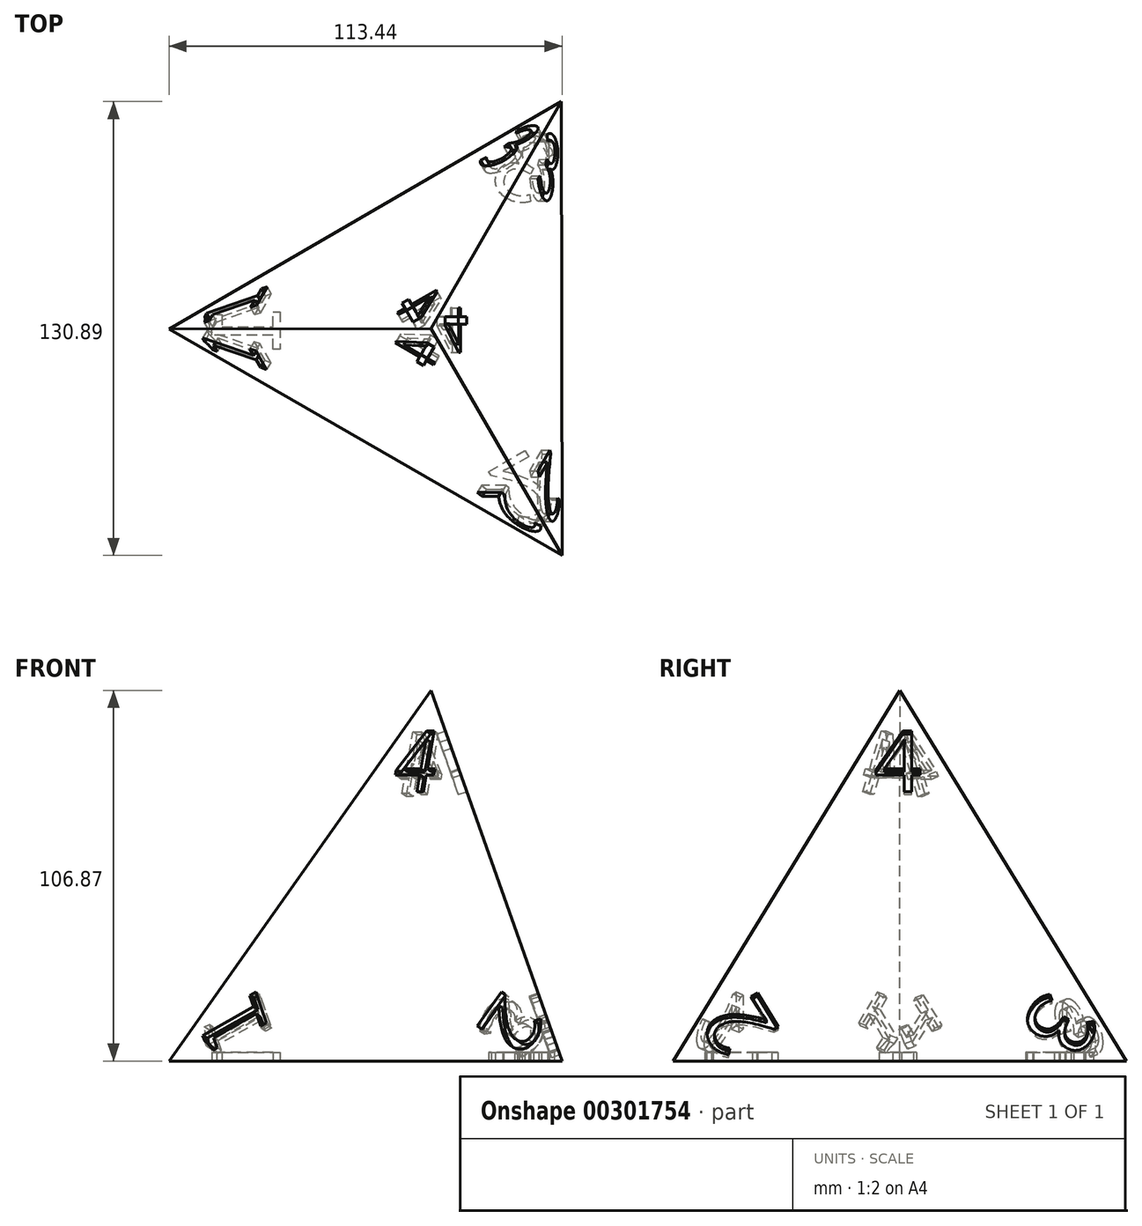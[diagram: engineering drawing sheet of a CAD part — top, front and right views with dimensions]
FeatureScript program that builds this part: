
annotation { "Feature Type Name" : "Feature", "Feature Type Description" : "" }
export const myFeature = defineFeature(function(context is Context, id is Id, definition is map)
    precondition{}
    {
        {
            var Q0;
            Q0=qCreatedBy(makeId("Top.planeOp"),FACE);
            var sketch = newSketch(context, id + "F0", { "sketchPlane" : qUnion([Q0])});
            skCircle(sketch, "E0.cCircle", {"center": v(0, 0) * mm, "radius": 75.57 * mm, "construction": true});
            skLineSegment(sketch, "E0.0", {"start": v(37.87, -65.4) * mm, "end": v(-75.57, -0.1) * mm});
            skLineSegment(sketch, "E0.1", {"start": v(-75.57, -0.1) * mm, "end": v(37.7, 65.5) * mm});
            skLineSegment(sketch, "E0.2", {"start": v(37.7, 65.5) * mm, "end": v(37.87, -65.4) * mm});
            skSolve(sketch);
        }
        {
            var Q0;
            Q0=qCreatedBy(makeId("Top.planeOp"),FACE);
            cPlane(context, id + "F1", {"entities" : qUnion([Q0]), "cplaneType" : CPlaneType.OFFSET, "offset" : 113.36 * mm, "width" : 152.4 * mm, "height" : 152.4 * mm});
        }
        {
            var Q0;
            Q0 = qSketchRegion(id + "F0", true);
            extrude(context, id + "F2", {"entities" : qUnion([Q0]), "depth" : 127 * mm, "hasDraft" : true, "draftAngle" : 19.47 * degree, "draftPullDirection" : true});
        }
        {
            var Q0;
            Q0=makeQuery(id+"F2.opExtrude","SWEPT_FACE",FACE,{"disambiguationData":[OSD([sQuery(id+"F0.wireOp",EDGE,"E0.2")])]});
            var sketch = newSketch(context, id + "F3", { "sketchPlane" : qUnion([Q0])});
            skText(sketch, "E1", { "text": "3", "fontName": "NotoSansCJKkr-Regular.otf"});
            skText(sketch, "E2", { "text": "4", "fontName": "NotoSansCJKkr-Regular.otf"});
            skText(sketch, "E3", { "text": "2", "fontName": "NotoSansCJKkr-Regular.otf"});
            const initialGuessF3  = {"E1": [0.04163, 0.00963, -0.49963, -0.86624, 0.01902], "E2": [-0.00737, 0.06982, 1, 0, 0.01824], "E3": [-0.03448, -0.0032, -0.50037, 0.86581, 0.01882]};
            skSetInitialGuess(sketch, initialGuessF3);
            skSolve(sketch);
        }
        {
            var Q0;
            Q0 = qSketchRegion(id + "F3", true);
            extrude(context, id + "F4", {"entities" : qUnion([Q0]), "operationType" : NewBodyOperationType.REMOVE, "oppositeDirection" : true, "depth" : 2.54 * mm});
        }
        {
            var Q0;
            Q0=makeQuery(id+"F2.opExtrude","CAP_FACE",FACE,{"disambiguationData":[OSD([sQuery(id+"F0.wireOp",EDGE,"E0.0"),sQuery(id+"F0.wireOp",EDGE,"E0.1"),sQuery(id+"F0.wireOp",EDGE,"E0.2")])],"isStart":true});
            var sketch = newSketch(context, id + "F5", { "sketchPlane" : qUnion([Q0])});
            skText(sketch, "E4", { "text": "1", "fontName": "NotoSansCJKkr-Regular.otf"});
            skText(sketch, "E5", { "text": "2", "fontName": "NotoSansCJKkr-Regular.otf"});
            skText(sketch, "E6", { "text": "3\n", "fontName": "NotoSansCJKkr-Regular.otf"});
            const initialGuessF5  = {"E4": [-0.04353, -0.00726, 0, 1, 0.01934], "E5": [0.01573, 0.0418, 0.8654, -0.5011, 0.01882], "E6": [0.02823, -0.03434, -0.86666, -0.4989, 0.01902]};
            skSetInitialGuess(sketch, initialGuessF5);
            skSolve(sketch);
        }
        {
            var Q0;
            Q0 = qSketchRegion(id + "F5", true);
            extrude(context, id + "F6", {"entities" : qUnion([Q0]), "operationType" : NewBodyOperationType.REMOVE, "oppositeDirection" : true, "depth" : 2.54 * mm});
        }
        {
            var Q0;
            Q0=makeQuery(id+"F2.opExtrude","SWEPT_FACE",FACE,{"disambiguationData":[OSD([sQuery(id+"F0.wireOp",EDGE,"E0.0")])]});
            var sketch = newSketch(context, id + "F7", { "sketchPlane" : qUnion([Q0])});
            skText(sketch, "E7", { "text": "2", "fontName": "NotoSansCJKkr-Regular.otf"});
            skText(sketch, "E8", { "text": "1", "fontName": "NotoSansCJKkr-Regular.otf"});
            skText(sketch, "E9", { "text": "4", "fontName": "NotoSansCJKkr-Regular.otf"});
            const initialGuessF7  = {"E7": [0.04286, 0.00147, -0.65424, -0.75628, 0.01882], "E8": [-0.03397, 0.00354, -0.32784, 0.94473, 0.01934], "E9": [0.00596, 0.06995, 0.98208, -0.18845, 0.01824]};
            skSetInitialGuess(sketch, initialGuessF7);
            skSolve(sketch);
        }
        {
            var Q0;
            Q0 = qSketchRegion(id + "F7", true);
            extrude(context, id + "F8", {"entities" : qUnion([Q0]), "operationType" : NewBodyOperationType.REMOVE, "oppositeDirection" : true, "depth" : 2.54 * mm});
        }
        {
            var Q0;
            Q0=makeQuery(id+"F2.opExtrude","SWEPT_FACE",FACE,{"disambiguationData":[OSD([sQuery(id+"F0.wireOp",EDGE,"E0.1")])]});
            var sketch = newSketch(context, id + "F9", { "sketchPlane" : qUnion([Q0])});
            skText(sketch, "E10", { "text": "4", "fontName": "NotoSansCJKkr-Regular.otf"});
            skText(sketch, "E11", { "text": "1", "fontName": "NotoSansCJKkr-Regular.otf"});
            skText(sketch, "E12", { "text": "3", "fontName": "NotoSansCJKkr-Regular.otf"});
            const initialGuessF9  = {"E10": [-0.02046, 0.06658, 0.98188, 0.18952, 0.01858], "E11": [0.03876, 0.01744, -0.32681, -0.94509, 0.01934], "E12": [-0.0331, -0.00953, -0.65506, 0.75557, 0.01902]};
            skSetInitialGuess(sketch, initialGuessF9);
            skSolve(sketch);
        }
        {
            var Q0;
            Q0 = qSketchRegion(id + "F9", true);
            extrude(context, id + "F10", {"entities" : qUnion([Q0]), "operationType" : NewBodyOperationType.REMOVE, "oppositeDirection" : true, "depth" : 2.54 * mm});
        }
    });
